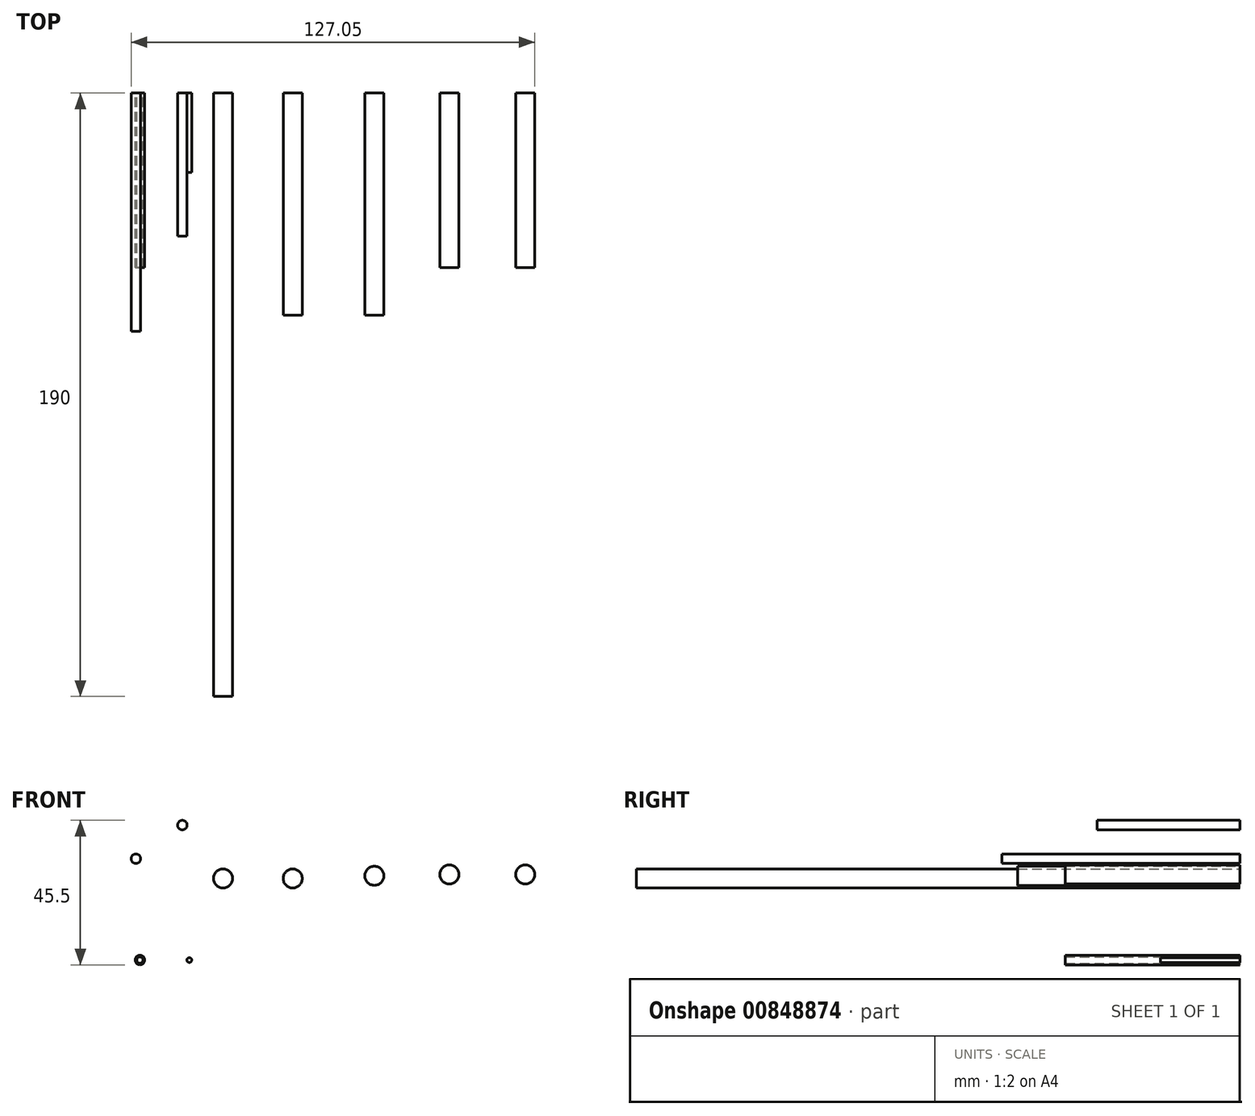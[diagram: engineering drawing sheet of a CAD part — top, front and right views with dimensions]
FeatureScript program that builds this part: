
annotation { "Feature Type Name" : "Feature", "Feature Type Description" : "" }
export const myFeature = defineFeature(function(context is Context, id is Id, definition is map)
    precondition{}
    {
        {
            var Q0;
            Q0=qCreatedBy(makeId("Front.planeOp"),FACE);
            var sketch = newSketch(context, id + "F0", { "sketchPlane" : qUnion([Q0])});
            skCircle(sketch, "E0", {"center": v(-33.02, 29.62) * mm, "radius": 3 * mm});
            skCircle(sketch, "E1", {"center": v(-11.08, 29.62) * mm, "radius": 3 * mm});
            skCircle(sketch, "E2", {"center": v(14.62, 30.45) * mm, "radius": 3 * mm});
            skCircle(sketch, "E3", {"center": v(38.23, 30.87) * mm, "radius": 3 * mm});
            skCircle(sketch, "E4", {"center": v(62.12, 30.87) * mm, "radius": 3 * mm});
            skCircle(sketch, "E5", {"center": v(-60.43, 35.83) * mm, "radius": 1.5 * mm});
            skCircle(sketch, "E6", {"center": v(-45.82, 46.42) * mm, "radius": 1.5 * mm});
            skCircle(sketch, "E7", {"center": v(-59.19, 3.92) * mm, "radius": 1 * mm});
            skCircle(sketch, "E8", {"center": v(-59.19, 3.92) * mm, "radius": 1.5 * mm});
            skCircle(sketch, "E9", {"center": v(-43.63, 3.92) * mm, "radius": 0.75 * mm});
            skSolve(sketch);
        }
        {
            var Q0;
            Q0=makeQuery(id+"F0.imprint","IMPRINT",FACE,{"disambiguationData":[TD([[makeQuery(id+"F0.imprint","IMPRINT",EDGE,{"derivedFrom":sQuery(id+"F0.wireOp",EDGE,"E0")}),1.0]])]});
            extrude(context, id + "F1", {"entities" : qUnion([Q0]), "depth" : 190 * mm, "offsetDistance" : 25 * mm});
        }
        {
            var Q0;
            Q0=makeQuery(id+"F0.imprint","IMPRINT",FACE,{"disambiguationData":[TD([[makeQuery(id+"F0.imprint","IMPRINT",EDGE,{"derivedFrom":sQuery(id+"F0.wireOp",EDGE,"E1")}),1.0]])]});
            var Q1;
            Q1=makeQuery(id+"F0.imprint","IMPRINT",FACE,{"disambiguationData":[TD([[makeQuery(id+"F0.imprint","IMPRINT",EDGE,{"derivedFrom":sQuery(id+"F0.wireOp",EDGE,"E2")}),1.0]])]});
            extrude(context, id + "F2", {"entities" : qUnion([Q0, Q1]), "depth" : 70 * mm, "offsetDistance" : 25 * mm});
        }
        {
            var Q0;
            Q0=makeQuery(id+"F0.imprint","IMPRINT",FACE,{"disambiguationData":[TD([[makeQuery(id+"F0.imprint","IMPRINT",EDGE,{"derivedFrom":sQuery(id+"F0.wireOp",EDGE,"E3")}),1.0]])]});
            extrude(context, id + "F3", {"entities" : qUnion([Q0]), "depth" : 55 * mm, "offsetDistance" : 25 * mm});
        }
        {
            var Q0;
            Q0=makeQuery(id+"F0.imprint","IMPRINT",FACE,{"disambiguationData":[TD([[makeQuery(id+"F0.imprint","IMPRINT",EDGE,{"derivedFrom":sQuery(id+"F0.wireOp",EDGE,"E4")}),1.0]])]});
            extrude(context, id + "F4", {"entities" : qUnion([Q0]), "depth" : 55 * mm, "offsetDistance" : 25 * mm});
        }
        {
            var Q0;
            Q0=makeQuery(id+"F0.imprint","IMPRINT",FACE,{"disambiguationData":[TD([[makeQuery(id+"F0.imprint","IMPRINT",EDGE,{"derivedFrom":sQuery(id+"F0.wireOp",EDGE,"E5")}),1.0]])]});
            extrude(context, id + "F5", {"entities" : qUnion([Q0]), "depth" : 75 * mm, "offsetDistance" : 25 * mm});
        }
        {
            var Q0;
            Q0=makeQuery(id+"F0.imprint","IMPRINT",FACE,{"disambiguationData":[TD([[makeQuery(id+"F0.imprint","IMPRINT",EDGE,{"derivedFrom":sQuery(id+"F0.wireOp",EDGE,"E6")}),1.0]])]});
            extrude(context, id + "F6", {"entities" : qUnion([Q0]), "depth" : 45 * mm, "offsetDistance" : 25 * mm});
        }
        {
            var Q0;
            Q0=makeQuery(id+"F0.imprint","IMPRINT",FACE,{"disambiguationData":[TD([[makeQuery(id+"F0.imprint","IMPRINT",EDGE,{"derivedFrom":sQuery(id+"F0.wireOp",EDGE,"E7")}),-1.0]])]});
            extrude(context, id + "F7", {"entities" : qUnion([Q0]), "depth" : 55 * mm, "offsetDistance" : 25 * mm});
        }
        {
            var Q0;
            Q0=makeQuery(id+"F0.imprint","IMPRINT",FACE,{"disambiguationData":[TD([[makeQuery(id+"F0.imprint","IMPRINT",EDGE,{"derivedFrom":sQuery(id+"F0.wireOp",EDGE,"E9")}),1.0]])]});
            extrude(context, id + "F8", {"entities" : qUnion([Q0]), "depth" : 25 * mm, "offsetDistance" : 25 * mm});
        }
    });
